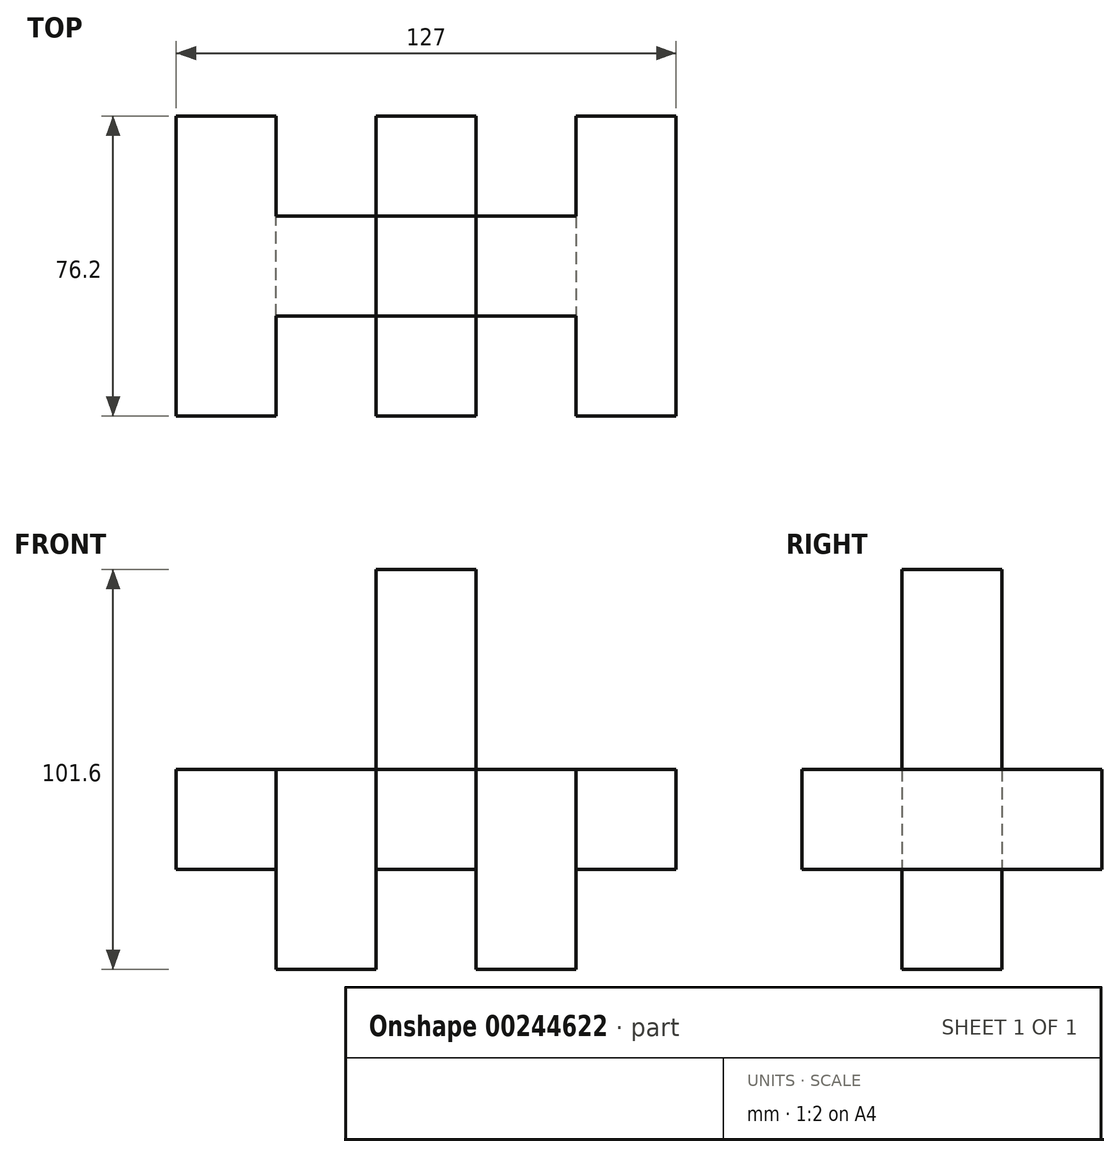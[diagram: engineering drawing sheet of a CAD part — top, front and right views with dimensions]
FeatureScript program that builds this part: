
annotation { "Feature Type Name" : "Feature", "Feature Type Description" : "" }
export const myFeature = defineFeature(function(context is Context, id is Id, definition is map)
    precondition{}
    {
        {
            var Q0;
            Q0=qCreatedBy(makeId("Top.planeOp"),FACE);
            var sketch = newSketch(context, id + "F0", { "sketchPlane" : qUnion([Q0])});
            skLineSegment(sketch, "E0.bottom", {"start": v(63.5, 12.7) * mm, "end": v(-63.5, 12.7) * mm});
            skLineSegment(sketch, "E0.top", {"start": v(63.5, -12.7) * mm, "end": v(-63.5, -12.7) * mm});
            skLineSegment(sketch, "E0.left", {"start": v(63.5, 12.7) * mm, "end": v(63.5, -12.7) * mm});
            skLineSegment(sketch, "E0.right", {"start": v(-63.5, 12.7) * mm, "end": v(-63.5, -12.7) * mm});
            skPoint(sketch, "E0.middle", {"position": v(0, 0) * mm});
            skLineSegment(sketch, "E1", {"start": v(-63.5, 12.7) * mm, "end": v(-63.5, 38.1) * mm});
            skLineSegment(sketch, "E2", {"start": v(-63.5, 38.1) * mm, "end": v(-38.1, 38.1) * mm});
            skLineSegment(sketch, "E3", {"start": v(-38.1, 38.1) * mm, "end": v(-38.1, 12.7) * mm});
            skLineSegment(sketch, "E4", {"start": v(-12.7, 38.1) * mm, "end": v(12.7, 38.1) * mm});
            skLineSegment(sketch, "E5", {"start": v(38.1, 38.1) * mm, "end": v(63.5, 38.1) * mm});
            skLineSegment(sketch, "E6", {"start": v(63.5, 38.1) * mm, "end": v(63.5, 12.7) * mm});
            skLineSegment(sketch, "E7", {"start": v(38.1, 38.1) * mm, "end": v(38.1, 12.7) * mm});
            skLineSegment(sketch, "E8", {"start": v(12.7, 38.1) * mm, "end": v(12.7, 12.7) * mm});
            skLineSegment(sketch, "E9", {"start": v(-12.7, 38.1) * mm, "end": v(-12.7, 12.7) * mm});
            skLineSegment(sketch, "E10", {"start": v(-63.5, -12.7) * mm, "end": v(-63.5, -38.1) * mm});
            skLineSegment(sketch, "E11", {"start": v(-63.5, -38.1) * mm, "end": v(-38.1, -38.1) * mm});
            skLineSegment(sketch, "E12", {"start": v(-38.1, -38.1) * mm, "end": v(-38.1, -12.7) * mm});
            skLineSegment(sketch, "E13", {"start": v(-12.7, -38.1) * mm, "end": v(12.7, -38.1) * mm});
            skLineSegment(sketch, "E14", {"start": v(38.1, -38.1) * mm, "end": v(63.5, -38.1) * mm});
            skLineSegment(sketch, "E15", {"start": v(63.5, -38.1) * mm, "end": v(63.5, -12.7) * mm});
            skLineSegment(sketch, "E16", {"start": v(-12.7, -38.1) * mm, "end": v(-12.7, -12.7) * mm});
            skLineSegment(sketch, "E17", {"start": v(12.7, -38.1) * mm, "end": v(12.7, -12.7) * mm});
            skLineSegment(sketch, "E18", {"start": v(38.1, -38.1) * mm, "end": v(38.1, -12.7) * mm});
            skSolve(sketch);
        }
        {
            var Q0;
            Q0 = qSketchRegion(id + "F0", true);
            extrude(context, id + "F1", {"entities" : qUnion([Q0]), "depth" : 25.4 * mm});
        }
        {
            var Q0;
            Q0=makeQuery(id+"F1.opExtrude","CAP_FACE",FACE,{"disambiguationData":[OSD([sQuery(id+"F0.wireOp",EDGE,"E0.bottom"),sQuery(id+"F0.wireOp",EDGE,"E0.top"),sQuery(id+"F0.wireOp",EDGE,"E0.left"),sQuery(id+"F0.wireOp",EDGE,"E0.right"),sQuery(id+"F0.wireOp",EDGE,"E1"),sQuery(id+"F0.wireOp",EDGE,"E2"),sQuery(id+"F0.wireOp",EDGE,"E3"),sQuery(id+"F0.wireOp",EDGE,"E4"),sQuery(id+"F0.wireOp",EDGE,"E5"),sQuery(id+"F0.wireOp",EDGE,"E6"),sQuery(id+"F0.wireOp",EDGE,"E7"),sQuery(id+"F0.wireOp",EDGE,"E8"),sQuery(id+"F0.wireOp",EDGE,"E9"),sQuery(id+"F0.wireOp",EDGE,"E10"),sQuery(id+"F0.wireOp",EDGE,"E11"),sQuery(id+"F0.wireOp",EDGE,"E12"),sQuery(id+"F0.wireOp",EDGE,"E13"),sQuery(id+"F0.wireOp",EDGE,"E14"),sQuery(id+"F0.wireOp",EDGE,"E15"),sQuery(id+"F0.wireOp",EDGE,"E16"),sQuery(id+"F0.wireOp",EDGE,"E17"),sQuery(id+"F0.wireOp",EDGE,"E18")])],"isStart":false});
            var sketch = newSketch(context, id + "F2", { "sketchPlane" : qUnion([Q0])});
            skLineSegment(sketch, "E19", {"start": v(-12.7, 12.7) * mm, "end": v(-12.7, -12.7) * mm});
            skLineSegment(sketch, "E20", {"start": v(-12.7, -12.7) * mm, "end": v(-13.78, -13.06) * mm});
            skLineSegment(sketch, "E21", {"start": v(12.7, -12.7) * mm, "end": v(-12.7, -12.7) * mm});
            skLineSegment(sketch, "E22", {"start": v(12.7, 12.7) * mm, "end": v(12.7, -12.7) * mm});
            skLineSegment(sketch, "E23", {"start": v(12.7, 12.7) * mm, "end": v(-12.7, 12.7) * mm});
            skSolve(sketch);
        }
        {
            var Q0;
            Q0=makeQuery(id+"F2.imprint","IMPRINT",FACE,{"disambiguationData":[TD([[makeQuery(id+"F2.imprint","IMPRINT",EDGE,{"derivedFrom":sQuery(id+"F2.wireOp",EDGE,"E19")}),1.0]])]});
            extrude(context, id + "F3", {"entities" : qUnion([Q0]), "operationType" : NewBodyOperationType.ADD, "depth" : 50.8 * mm});
        }
        {
            var Q0;
            Q0=makeQuery(id+"F1.opExtrude","CAP_FACE",FACE,{"disambiguationData":[OSD([sQuery(id+"F0.wireOp",EDGE,"E0.bottom"),sQuery(id+"F0.wireOp",EDGE,"E0.top"),sQuery(id+"F0.wireOp",EDGE,"E0.left"),sQuery(id+"F0.wireOp",EDGE,"E0.right"),sQuery(id+"F0.wireOp",EDGE,"E1"),sQuery(id+"F0.wireOp",EDGE,"E2"),sQuery(id+"F0.wireOp",EDGE,"E3"),sQuery(id+"F0.wireOp",EDGE,"E4"),sQuery(id+"F0.wireOp",EDGE,"E5"),sQuery(id+"F0.wireOp",EDGE,"E6"),sQuery(id+"F0.wireOp",EDGE,"E7"),sQuery(id+"F0.wireOp",EDGE,"E8"),sQuery(id+"F0.wireOp",EDGE,"E9"),sQuery(id+"F0.wireOp",EDGE,"E10"),sQuery(id+"F0.wireOp",EDGE,"E11"),sQuery(id+"F0.wireOp",EDGE,"E12"),sQuery(id+"F0.wireOp",EDGE,"E13"),sQuery(id+"F0.wireOp",EDGE,"E14"),sQuery(id+"F0.wireOp",EDGE,"E15"),sQuery(id+"F0.wireOp",EDGE,"E16"),sQuery(id+"F0.wireOp",EDGE,"E17"),sQuery(id+"F0.wireOp",EDGE,"E18")])],"isStart":true});
            var sketch = newSketch(context, id + "F4", { "sketchPlane" : qUnion([Q0])});
            skLineSegment(sketch, "E24", {"start": v(-38.1, 12.7) * mm, "end": v(-38.1, -12.7) * mm});
            skLineSegment(sketch, "E25", {"start": v(-38.1, -12.7) * mm, "end": v(-12.7, -12.7) * mm});
            skLineSegment(sketch, "E26", {"start": v(-12.7, -12.7) * mm, "end": v(-12.7, 12.7) * mm});
            skLineSegment(sketch, "E27", {"start": v(-12.7, 12.7) * mm, "end": v(-38.1, 12.7) * mm});
            skLineSegment(sketch, "E28", {"start": v(12.7, 12.7) * mm, "end": v(12.7, -12.7) * mm});
            skLineSegment(sketch, "E29", {"start": v(12.7, -12.7) * mm, "end": v(38.1, -12.7) * mm});
            skLineSegment(sketch, "E30", {"start": v(38.1, -12.7) * mm, "end": v(38.1, 12.7) * mm});
            skLineSegment(sketch, "E31", {"start": v(38.1, 12.7) * mm, "end": v(12.7, 12.7) * mm});
            skSolve(sketch);
        }
        {
            var Q0;
            Q0 = qSketchRegion(id + "F4", true);
            extrude(context, id + "F5", {"entities" : qUnion([Q0]), "operationType" : NewBodyOperationType.ADD, "depth" : 25.4 * mm});
        }
    });
